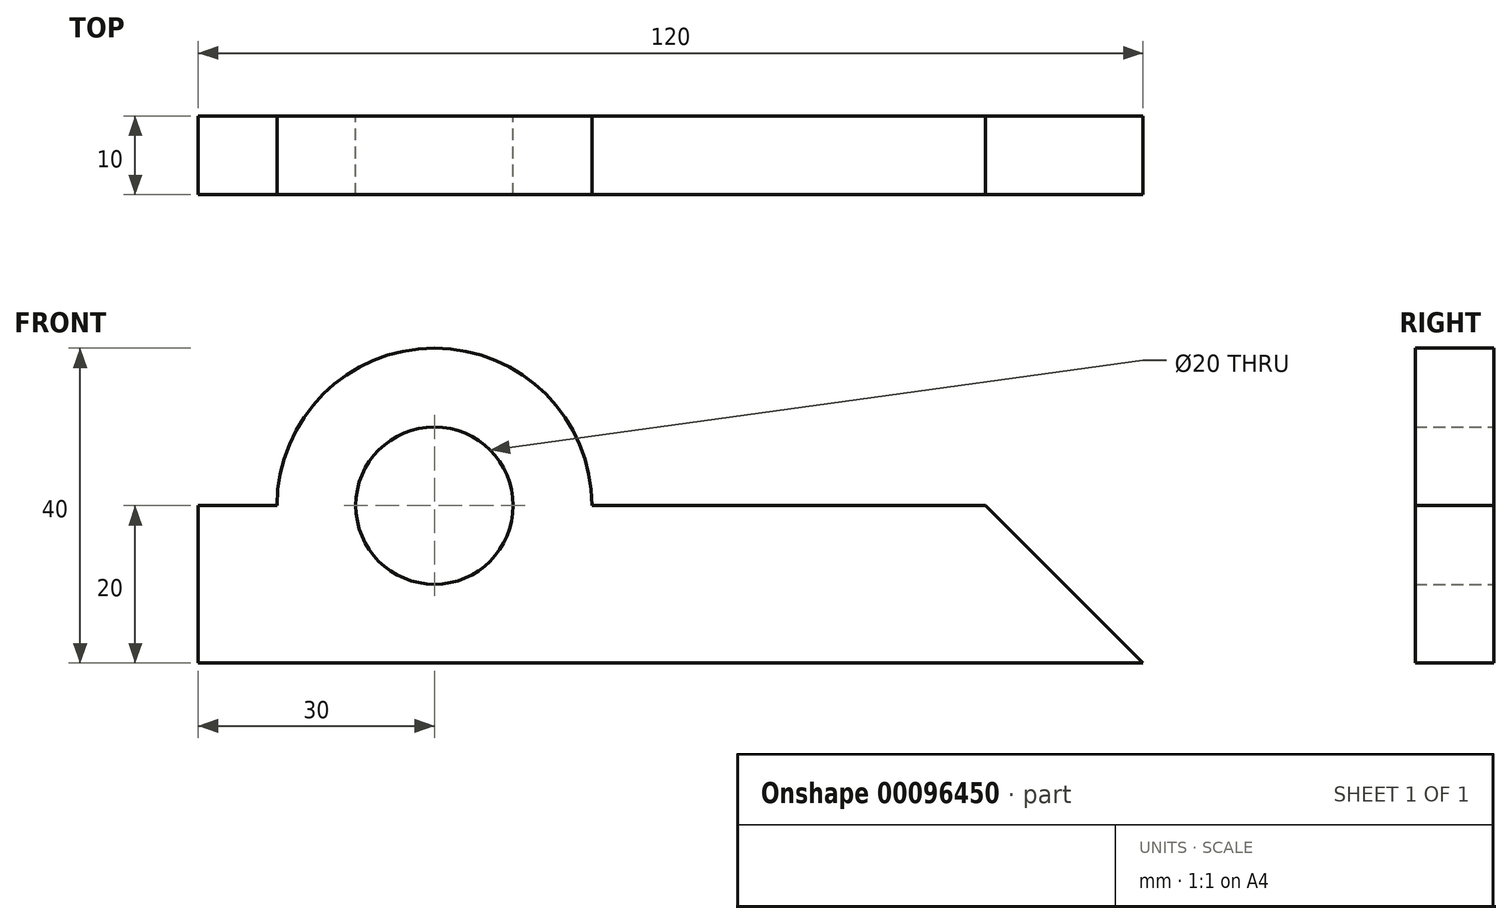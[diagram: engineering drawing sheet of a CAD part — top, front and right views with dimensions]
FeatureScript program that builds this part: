
annotation { "Feature Type Name" : "Feature", "Feature Type Description" : "" }
export const myFeature = defineFeature(function(context is Context, id is Id, definition is map)
    precondition{}
    {
        {
            var Q0;
            Q0=qCreatedBy(makeId("Front.planeOp"),FACE);
            var sketch = newSketch(context, id + "F0", { "sketchPlane" : qUnion([Q0])});
            skLineSegment(sketch, "E0", {"start": v(0, 0) * mm, "end": v(120, 0) * mm});
            skLineSegment(sketch, "E1", {"start": v(120, 0) * mm, "end": v(100, 20) * mm});
            skLineSegment(sketch, "E2", {"start": v(100, 20) * mm, "end": v(50, 20) * mm});
            skLineSegment(sketch, "E3", {"start": v(0, 0) * mm, "end": v(0, 20) * mm});
            skLineSegment(sketch, "E4", {"start": v(0, 20) * mm, "end": v(10, 20) * mm});
            skLineSegment(sketch, "E5", {"start": v(10, 20) * mm, "end": v(50, 20) * mm, "construction": true});
            skCircle(sketch, "E6", {"center": v(30, 20) * mm, "radius": 10 * mm});
            skArc(sketch, "E7", {"start": v(10, 20) * mm, "mid": v(30, 40) * mm, "end": v(50, 20) * mm});
            skSolve(sketch);
        }
        {
            var Q0;
            Q0=makeQuery(id+"F0.imprint","IMPRINT",FACE,{"disambiguationData":[TD([[makeQuery(id+"F0.imprint","IMPRINT",EDGE,{"derivedFrom":sQuery(id+"F0.wireOp",EDGE,"E0")}),1.0]])]});
            extrude(context, id + "F1", {"entities" : qUnion([Q0]), "depth" : 10 * mm});
        }
    });
